# Revit family: Glowica_natryskowa_wandaloodporna_z_regulacja_nachylenia
name_source: partatom
category: Osprzęt hydrauliczny
units: mm (PartAtom-declared; Revit-internal decimal feet)

## family parameters
Obiekt nadrzędny = Powierzchnia
Punkt obliczania pomieszczeń = Nie
Tnij formami wycięć po wczytaniu = Nie
Typ części = Normalny
Współdzielony = Nie
Wymiar okrągłego złącza = Użyj średnicy

## types (1)
- FAN6000
    Depth / Glebokosc = 78 mm  [stored 0.255906 ft]
    Domyślna rzędna = 1219 mm
    Height / Wysokosc = 68 mm
    Komentarze do typu = Głowica natryskowa wandaloodporna z regulacją nachylenia
    Manufacturer code / Kod producenta = 5901764294108
    Material finish / Wykonczenie = Mosiądz pokryty chromem
    Opis = Głowica pryszynicowa z regulowaną głowicą to idealna rozwiązanie do zastosowania w natryskach w obiektach użytku publicznego. Dzięki wandaloodpornemu wykonaniu jest bezpieczna dla użytkowników i jednocześnie bardzo trwała na uszkodzenia mechaniczne. Dobierając wyposażenie pływalni czy łazienek publicznych zdecydowanie warto wybrać głowicę prysznicową wykonaną z mosiądzu na wodę zimna lub zmieszaną.
    Producent = faneco.com
    Product code / Kod produktu = FAN6000
    URL = https://faneco.com
    Weight / Waga = 0.46 kg
    Width / Szerokosc = 43 mm  [stored 0.141076 ft]

note: [stored X ft] marks values corroborated as IEEE doubles in the binary element streams (Revit-internal decimal feet)

## geometry (parser evidence)
native form markers: Sweep x9
no freeform markers — native parametric forms only
